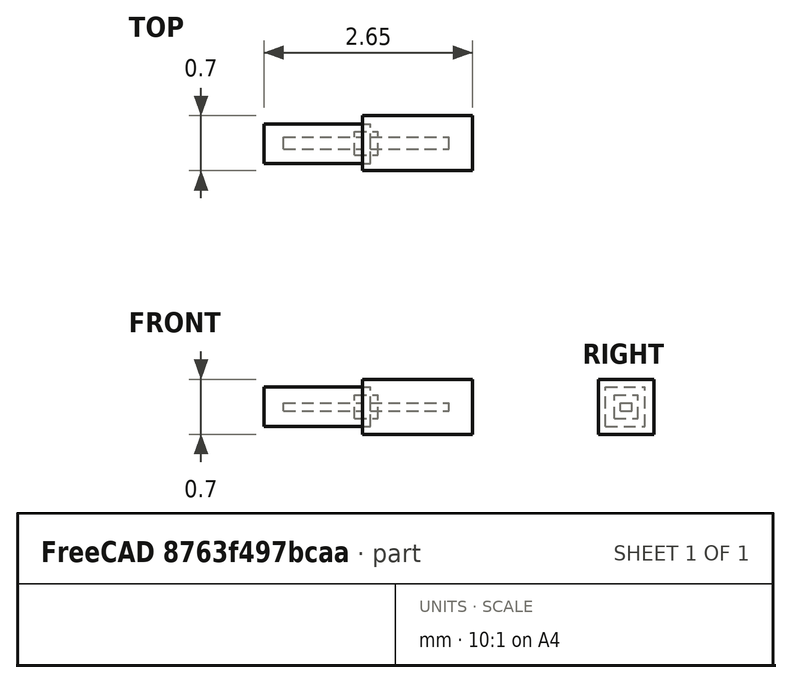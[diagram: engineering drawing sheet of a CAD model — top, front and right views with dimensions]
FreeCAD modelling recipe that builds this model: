
FCSTD DOCUMENT  (FreeCAD 1.0R39109 (Git))
Label: model
License: All rights reserved
LicenseURL: https://en.wikipedia.org/wiki/All_rights_reserved
objects: Part::Feature×6, Part::Box×5, Part::FeaturePython×4, App::DocumentObjectGroupPython×2
note: 15 computed .brp shape members not serialized (recipe doc carries the construction recipe); baked Part::Feature solids carry a one-line shape summary decoded from their .brp

FEATURE [Part::Box] Box  label="hullWall1"
  AttacherType = Attacher::AttachEngine3D
  Height = 0.1
  Length = 1
  Placement = pos=(0,-0.075,-0.05) rot=(0,0,1;0rad)
  Width = 0.15
FEATURE [Part::Box] Box001  label="hullWall2"
  AttacherType = Attacher::AttachEngine3D
  Height = 0.1
  Length = 1
  Placement = pos=(-1.1,-0.075,-0.05) rot=(0,0,1;0rad)
  Width = 0.15
FEATURE [Part::Feature] Face  label="outlet"
  Placement = pos=(-1.5,-0.5,-0.5) rot=(0,0,1;0rad)
  shape: bbox 2e-07 x 1 x 1 mm, 1 faces, 0 solids (baked)
FEATURE [Part::Feature] Face001  label="inlet"
  Placement = pos=(-1.5,-0.5,-0.5) rot=(0,0,1;0rad)
  shape: bbox 2e-07 x 1 x 1 mm, 1 faces, 0 solids (baked)
FEATURE [Part::Feature] Face002  label="front"
  Placement = pos=(-1.5,-0.5,-0.5) rot=(0,0,1;0rad)
  shape: bbox 5 x 2e-07 x 1 mm, 1 faces, 0 solids (baked)
FEATURE [Part::Feature] Face003  label="back"
  Placement = pos=(-1.5,-0.5,-0.5) rot=(0,0,1;0rad)
  shape: bbox 5 x 2e-07 x 1 mm, 1 faces, 0 solids (baked)
FEATURE [Part::Feature] Face004  label="base"
  Placement = pos=(-1.5,-0.5,-0.5) rot=(0,0,1;0rad)
  shape: bbox 5 x 1 x 2e-07 mm, 1 faces, 0 solids (baked)
FEATURE [Part::Feature] Face005  label="atomosphere"
  Placement = pos=(-1.5,-0.5,-0.5) rot=(0,0,1;0rad)
  shape: bbox 5 x 1 x 2e-07 mm, 1 faces, 0 solids (baked)
FEATURE [Part::Box] Box002  label="overset1"
  AttacherType = Attacher::AttachEngine3D
  Height = 0.7
  Length = 1.4
  Placement = pos=(-0.1,-0.35,-0.35) rot=(0,0,1;0rad)
  Width = 0.7
FEATURE [Part::Box] Box003  label="overset2"
  AttacherType = Attacher::AttachEngine3D
  Height = 0.5
  Length = 1.35
  Placement = pos=(-1.35,-0.26,-0.25) rot=(0,0,1;0rad)
  Width = 0.5
FEATURE [Part::FeaturePython] CfdSolver  # WARN: FeaturePython — macro-defined, semantics opaque (R4)
  Parallel = true
  ParallelCores = 1
  ParallelMethod = 0
FEATURE [Part::FeaturePython] MeshRefinement  # WARN: FeaturePython — macro-defined, semantics opaque (R4)
  AllowDiscont = true
  CellSize = 0.051
  ExpansionRatio = 1.2
  FirstLayerHeight = 0
  Internal = false
  KeepCell = false
  NumberLayers = 1
  RefinementLevel = 0
  RefinementThickness = 0
  RemoveCell = false
  ShapeRefs = -> [Box]
  patchType = 1
FEATURE [Part::FeaturePython] MeshRefinement001  # WARN: FeaturePython — macro-defined, semantics opaque (R4)
  AllowDiscont = true
  CellSize = 0.051
  ExpansionRatio = 1.2
  FirstLayerHeight = 0
  Internal = false
  KeepCell = false
  NumberLayers = 1
  RefinementLevel = 0
  RefinementThickness = 0
  RemoveCell = false
  ShapeRefs = -> [Box002]
  patchType = 3
FEATURE [Part::Box] Box004  label="fineRegion"
  AttacherType = Attacher::AttachEngine3D
  Height = 0.3
  Length = 0.3
  Placement = pos=(-0.2,-0.15,-0.15) rot=(0,0,1;0rad)
  Width = 0.3
FEATURE [Part::FeaturePython] MeshRefinement002  # WARN: FeaturePython — macro-defined, semantics opaque (R4)
  AllowDiscont = true
  CellSize = 0.0075
  ExpansionRatio = 1.2
  FirstLayerHeight = 0
  Internal = true
  KeepCell = false
  NumberLayers = 1
  RefinementLevel = 1
  RefinementThickness = 0
  RemoveCell = false
  ShapeRefs = -> [Box004]
  patchType = 0
FEATURE [App::DocumentObjectGroupPython] CFDMesh  # scripted group (container) (typed FeaturePython)
  BaseCellSize = 0.025
  ElementDimension = 1
  FeatureAngle = 30
  Group = -> [MeshRefinement,MeshRefinement001,MeshRefinement002]
  MeshUtility = 0
  ScaleToMeter = 1
  keepCellsIntersectingBoundary = false
  opt_featureSizeFactor = 0.4
  opt_maxNumIterations = 5
  opt_nSmoothNormals = 3
  opt_reCalculateNormals = true
  opt_relThicknessTol = 0.05
  optimiseLayer = false
  patchTypeSetting = false
  workflowControls = 0
FEATURE [App::DocumentObjectGroupPython] dexcsCfdAnalysis  # scripted group (container) (typed FeaturePython)
  Group = -> [CFDMesh,CfdSolver]
  IsActiveAnalysis = true
  NeedsCaseRewrite = true
  NeedsMeshRerun = true
  NeedsMeshRewrite = true
  PlotMaxnumber = 5000
  PlotMethodLast = false
